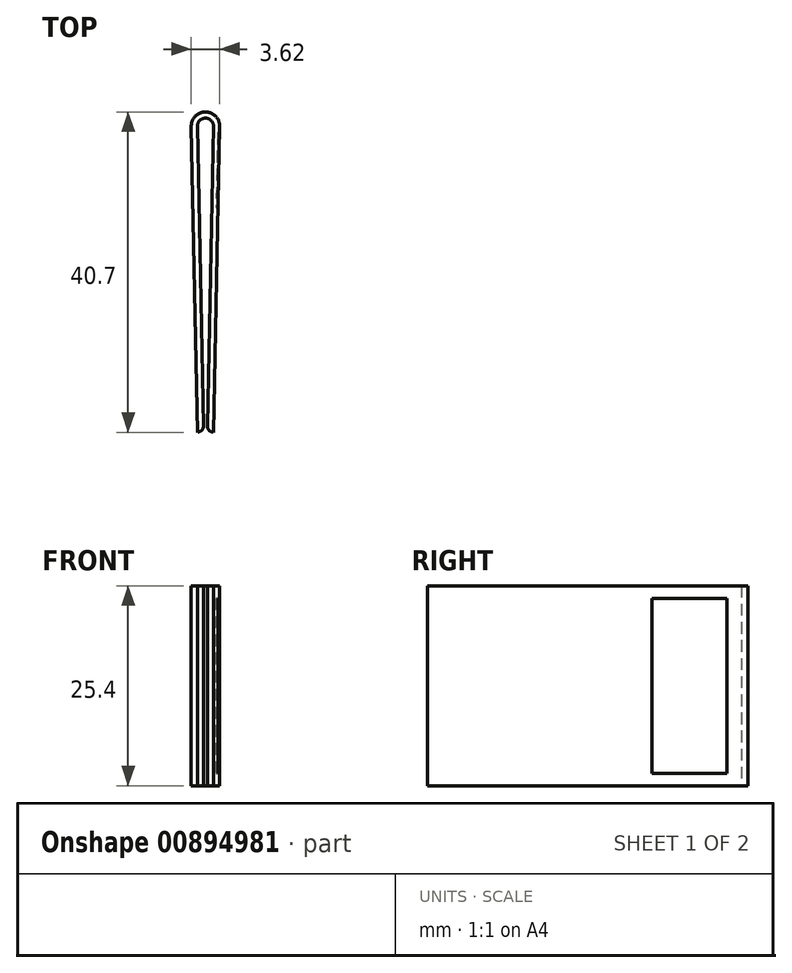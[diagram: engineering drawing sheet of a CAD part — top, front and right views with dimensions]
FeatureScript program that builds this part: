
annotation { "Feature Type Name" : "Feature", "Feature Type Description" : "" }
export const myFeature = defineFeature(function(context is Context, id is Id, definition is map)
    precondition{}
    {
        {
            var Q0;
            Q0=qCreatedBy(makeId("Top.planeOp"),FACE);
            var sketch = newSketch(context, id + "F0", { "sketchPlane" : qUnion([Q0])});
            skArc(sketch, "E0", {"start": v(1.02, -0.02) * mm, "mid": v(0, 1.02) * mm, "end": v(-1.02, -0.02) * mm});
            skArc(sketch, "E1", {"start": v(-1.03, -38.9) * mm, "mid": v(-0.48, -38.65) * mm, "end": v(-0.25, -38.08) * mm});
            skArc(sketch, "E2", {"start": v(0.25, -38.08) * mm, "mid": v(0.48, -38.65) * mm, "end": v(1.03, -38.9) * mm});
            skLineSegment(sketch, "E3", {"start": v(-1.02, -0.02) * mm, "end": v(-0.25, -38.08) * mm});
            skLineSegment(sketch, "E4", {"start": v(1.02, -0.02) * mm, "end": v(0.25, -38.08) * mm});
            skLineSegment(sketch, "E5", {"start": v(-1.05, -38.1) * mm, "end": v(-1.05, -38.9) * mm, "construction": true});
            skLineSegment(sketch, "E6", {"start": v(1.05, -38.1) * mm, "end": v(1.05, -38.9) * mm, "construction": true});
            skArc(sketch, "E7", {"start": v(1.8, -0.04) * mm, "mid": v(0, 1.8) * mm, "end": v(-1.8, -0.04) * mm});
            skLineSegment(sketch, "E8", {"start": v(-1.8, -0.04) * mm, "end": v(-1.03, -38.9) * mm});
            skLineSegment(sketch, "E9", {"start": v(1.03, -38.9) * mm, "end": v(1.8, -0.04) * mm});
            skPoint(sketch, "E10.orphan", {"position": v(-1.05, -38.08) * mm});
            skSolve(sketch);
        }
        {
            var Q0;
            Q0=makeQuery(id+"F0.imprint","IMPRINT",FACE,{"disambiguationData":[TD([[makeQuery(id+"F0.imprint","IMPRINT",EDGE,{"derivedFrom":sQuery(id+"F0.wireOp",EDGE,"E0")}),-1.0]])]});
            extrude(context, id + "F1", {"entities" : qUnion([Q0]), "depth" : 25.4 * mm, "offsetDistance" : 25.4 * mm});
        }
        {
            var Q0;
            Q0=makeQuery(id+"F1.opExtrude","SWEPT_FACE",FACE,{"disambiguationData":[OSD([sQuery(id+"F0.wireOp",EDGE,"E9")])]});
            var sketch = newSketch(context, id + "F2", { "sketchPlane" : qUnion([Q0])});
            skLineSegment(sketch, "E11.bottom", {"start": v(-0.8, 23.81) * mm, "end": v(-10.32, 23.81) * mm});
            skLineSegment(sketch, "E11.top", {"start": v(-0.8, 1.59) * mm, "end": v(-10.32, 1.59) * mm});
            skLineSegment(sketch, "E11.left", {"start": v(-0.8, 23.81) * mm, "end": v(-0.8, 1.59) * mm});
            skLineSegment(sketch, "E11.right", {"start": v(-10.32, 23.81) * mm, "end": v(-10.32, 1.59) * mm});
            skSolve(sketch);
        }
        {
            var Q0;
            Q0=makeQuery(id+"F2.imprint","IMPRINT",FACE,{"disambiguationData":[TD([[makeQuery(id+"F2.imprint","IMPRINT",EDGE,{"derivedFrom":sQuery(id+"F2.wireOp",EDGE,"E11.bottom")}),1.0]])]});
            extrude(context, id + "F3", {"entities" : qUnion([Q0]), "operationType" : NewBodyOperationType.REMOVE, "oppositeDirection" : true, "depth" : 0.25 * mm, "offsetDistance" : 25.4 * mm});
        }
    });
